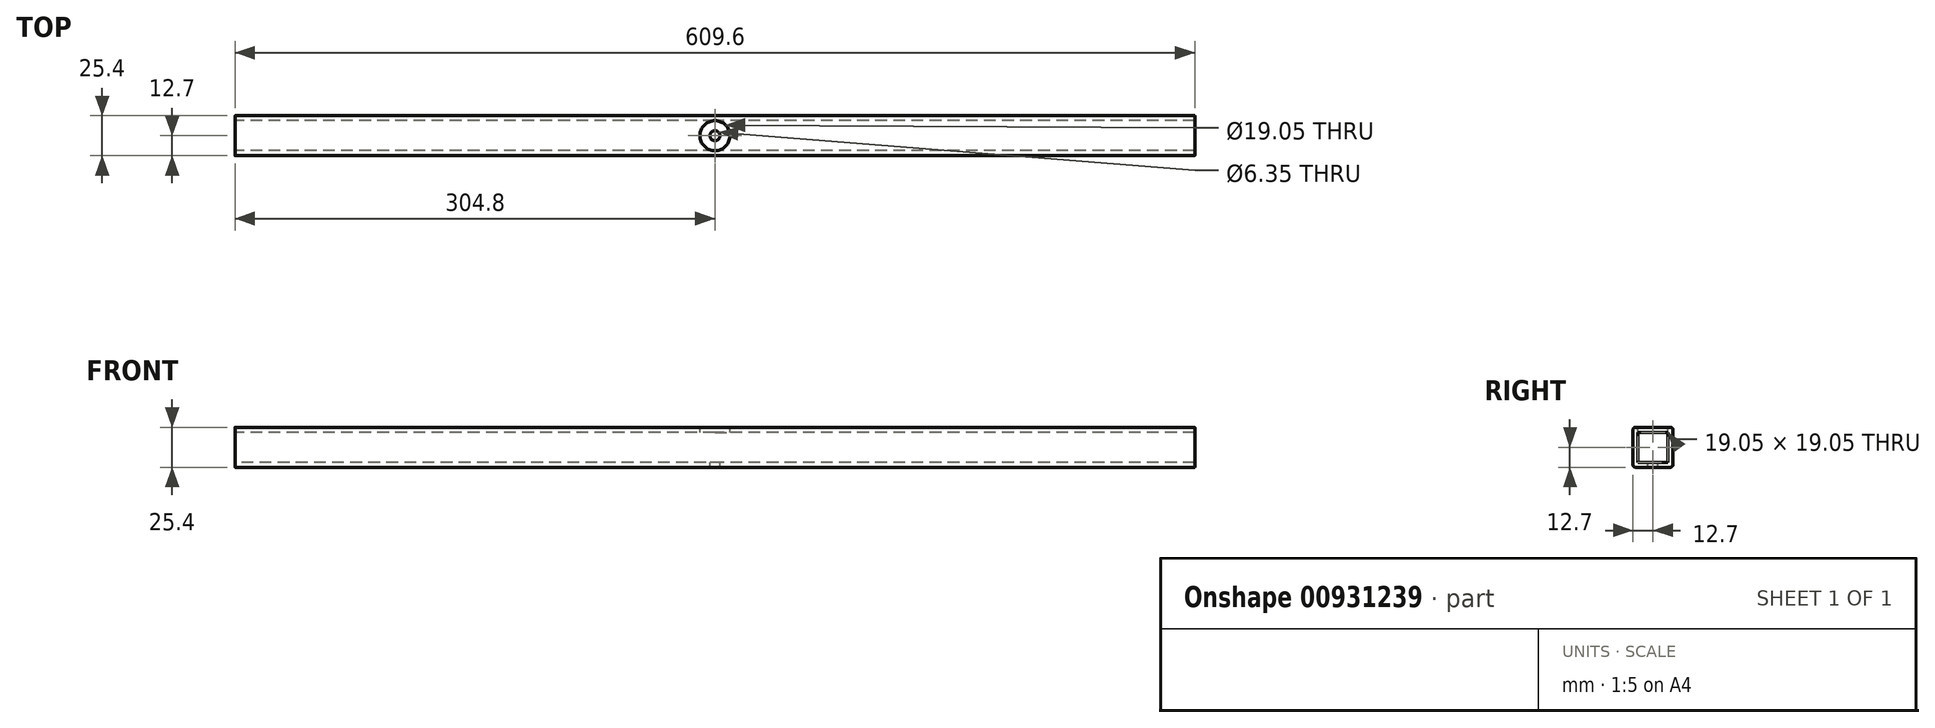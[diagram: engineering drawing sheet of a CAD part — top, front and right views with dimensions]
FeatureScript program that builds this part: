
annotation { "Feature Type Name" : "Feature", "Feature Type Description" : "" }
export const myFeature = defineFeature(function(context is Context, id is Id, definition is map)
    precondition{}
    {
        {
            var Q0;
            Q0=qCreatedBy(makeId("Right.planeOp"),FACE);
            var sketch = newSketch(context, id + "F0", { "sketchPlane" : qUnion([Q0])});
            skLineSegment(sketch, "E0.bottom", {"start": v(0, 0) * mm, "end": v(25.4, 0) * mm});
            skLineSegment(sketch, "E0.top", {"start": v(0, -25.4) * mm, "end": v(25.4, -25.4) * mm});
            skLineSegment(sketch, "E0.left", {"start": v(0, 0) * mm, "end": v(0, -25.4) * mm});
            skLineSegment(sketch, "E0.right", {"start": v(25.4, 0) * mm, "end": v(25.4, -25.4) * mm});
            skLineSegment(sketch, "E1.0", {"start": v(3.18, -3.18) * mm, "end": v(22.23, -3.18) * mm});
            skLineSegment(sketch, "E1.1", {"start": v(3.18, -3.18) * mm, "end": v(3.18, -22.23) * mm});
            skLineSegment(sketch, "E1.2", {"start": v(3.18, -22.23) * mm, "end": v(22.23, -22.23) * mm});
            skLineSegment(sketch, "E1.3", {"start": v(22.23, -3.18) * mm, "end": v(22.23, -22.23) * mm});
            skSolve(sketch);
        }
        {
            var Q0;
            Q0=makeQuery(id+"F0.imprint","IMPRINT",FACE,{"disambiguationData":[TD([[makeQuery(id+"F0.imprint","IMPRINT",EDGE,{"derivedFrom":sQuery(id+"F0.wireOp",EDGE,"E0.bottom")}),-1.0]])]});
            extrude(context, id + "F1", {"entities" : qUnion([Q0]), "depth" : 609.6 * mm, "offsetDistance" : 25.4 * mm});
        }
        {
            var Q0;
            Q0=makeQuery(id+"F1.opExtrude","SWEPT_EDGE",EDGE,{"disambiguationData":[OSD([sQuery(id+"F0.wireOp",EDGE,"E0.bottom"),sQuery(id+"F0.wireOp",EDGE,"E0.left")])]});
            var Q1;
            Q1=makeQuery(id+"F1.opExtrude","SWEPT_EDGE",EDGE,{"disambiguationData":[OSD([sQuery(id+"F0.wireOp",EDGE,"E0.bottom"),sQuery(id+"F0.wireOp",EDGE,"E0.right")])]});
            var Q2;
            Q2=makeQuery(id+"F1.opExtrude","SWEPT_EDGE",EDGE,{"disambiguationData":[OSD([sQuery(id+"F0.wireOp",EDGE,"E0.top"),sQuery(id+"F0.wireOp",EDGE,"E0.left")])]});
            var Q3;
            Q3=makeQuery(id+"F1.opExtrude","SWEPT_EDGE",EDGE,{"disambiguationData":[OSD([sQuery(id+"F0.wireOp",EDGE,"E0.top"),sQuery(id+"F0.wireOp",EDGE,"E0.right")])]});
            fillet(context, id + "F2", {"entities" : qUnion([Q0, Q1, Q2, Q3]), "radius" : 1.59 * mm, "tangentPropagation" : true, "allowEdgeOverflow" : false});
        }
        {
            var Q0;
            Q0=makeQuery(id+"F1.opExtrude","SWEPT_FACE",FACE,{"disambiguationData":[OSD([sQuery(id+"F0.wireOp",EDGE,"E0.bottom")])]});
            var sketch = newSketch(context, id + "F3", { "sketchPlane" : qUnion([Q0])});
            skCircle(sketch, "E2", {"center": v(304.8, 12.7) * mm, "radius": 9.53 * mm});
            skPoint(sketch, "E2.centerSnap0", {"position": v(304.8, 23.81) * mm});
            skSolve(sketch);
        }
        {
            var Q0;
            Q0 = qSketchRegion(id + "F3", true);
            extrude(context, id + "F4", {"entities" : qUnion([Q0]), "operationType" : NewBodyOperationType.REMOVE, "oppositeDirection" : true, "depth" : 6.35 * mm, "offsetDistance" : 25.4 * mm});
        }
        {
            var Q0;
            Q0=makeQuery(id+"F1.opExtrude","SWEPT_FACE",FACE,{"disambiguationData":[OSD([sQuery(id+"F0.wireOp",EDGE,"E0.bottom")])]});
            var sketch = newSketch(context, id + "F5", { "sketchPlane" : qUnion([Q0])});
            skCircle(sketch, "E3", {"center": v(304.8, 12.7) * mm, "radius": 3.18 * mm});
            skSolve(sketch);
        }
        {
            var Q0;
            Q0 = qSketchRegion(id + "F5", true);
            extrude(context, id + "F6", {"entities" : qUnion([Q0]), "operationType" : NewBodyOperationType.REMOVE, "oppositeDirection" : true, "depth" : 25.4 * mm, "offsetDistance" : 25.4 * mm});
        }
    });
